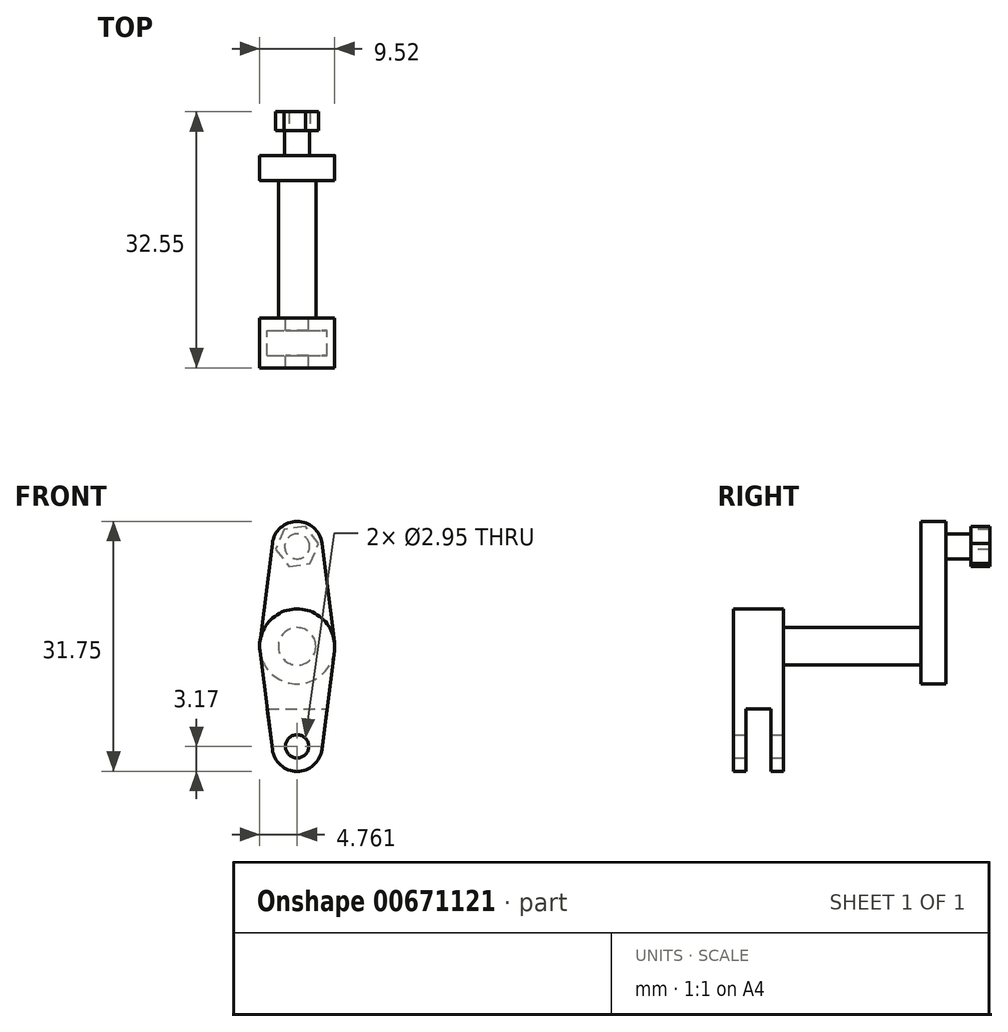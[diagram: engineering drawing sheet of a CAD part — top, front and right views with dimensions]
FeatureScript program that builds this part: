
annotation { "Feature Type Name" : "Feature", "Feature Type Description" : "" }
export const myFeature = defineFeature(function(context is Context, id is Id, definition is map)
    precondition{}
    {
        {
            var Q0;
            Q0=qCreatedBy(makeId("Front.planeOp"),FACE);
            var sketch = newSketch(context, id + "F0", { "sketchPlane" : qUnion([Q0])});
            skLineSegment(sketch, "E0.bottom", {"start": v(30.87, 50.07) * mm, "end": v(40.4, 50.07) * mm});
            skLineSegment(sketch, "E0.top", {"start": v(30.87, 15.15) * mm, "end": v(40.4, 15.15) * mm});
            skLineSegment(sketch, "E0.left", {"start": v(30.87, 50.07) * mm, "end": v(30.87, 15.15) * mm});
            skLineSegment(sketch, "E0.right", {"start": v(40.4, 50.07) * mm, "end": v(40.4, 15.15) * mm});
            skCircle(sketch, "E1", {"center": v(35.63, 45.31) * mm, "radius": 1.47 * mm});
            skCircle(sketch, "E2", {"center": v(35.63, 19.91) * mm, "radius": 1.47 * mm});
            skCircle(sketch, "E3", {"center": v(35.63, 32.61) * mm, "radius": 4.76 * mm});
            skCircle(sketch, "E4", {"center": v(35.63, 45.31) * mm, "radius": 3.18 * mm});
            skCircle(sketch, "E5", {"center": v(35.63, 19.91) * mm, "radius": 3.18 * mm});
            skLineSegment(sketch, "E6", {"start": v(32.48, 45.7) * mm, "end": v(30.9, 33.2) * mm});
            skLineSegment(sketch, "E7", {"start": v(38.78, 45.7) * mm, "end": v(40.36, 33.2) * mm});
            skLineSegment(sketch, "E8", {"start": v(30.9, 32.01) * mm, "end": v(32.48, 19.51) * mm});
            skLineSegment(sketch, "E9", {"start": v(40.36, 32.01) * mm, "end": v(38.78, 19.51) * mm});
            skSolve(sketch);
        }
        {
            var Q0;
            Q0=makeQuery(id+"F0.imprint","IMPRINT",FACE,{"disambiguationData":[TD([[makeQuery(id+"F0.imprint","IMPRINT",EDGE,{"derivedFrom":sQuery(id+"F0.wireOp",EDGE,"E1")}),1.0]])]});
            var Q1;
            Q1=makeQuery(id+"F0.imprint","IMPRINT",FACE,{"disambiguationData":[TD([[makeQuery(id+"F0.imprint","IMPRINT",EDGE,{"derivedFrom":sQuery(id+"F0.wireOp",EDGE,"E1")}),-1.0]])]});
            var Q2;
            {var subQ0=sQuery(id+"F0.wireOp",EDGE,"E6");Q2=makeQuery(id+"F0.imprint","IMPRINT",FACE,{"disambiguationData":[TD([[makeQuery(id+"F0.imprint","IMPRINT",EDGE,{"derivedFrom":subQ0}),1.0]])]});}
            var Q3;
            {var subQ0=sQuery(id+"F0.wireOp",EDGE,"E3");var subQ4=makeQuery(id+"F0.imprint","INTERSECT",VERTEX,{"derivedFrom":[subQ0,sQuery(id+"F0.wireOp",EDGE,"E7")]});Q3=makeQuery(id+"F0.imprint","IMPRINT",FACE,{"disambiguationData":[TD([[makeQuery(id+"F0.imprint","IMPRINT",EDGE,{"disambiguationData":[TD([[subQ4,1.0]])],"derivedFrom":subQ0}),1.0]])]});}
            extrude(context, id + "F1", {"entities" : qUnion([Q0, Q1, Q2, Q3]), "depth" : 3.17 * mm});
        }
        {
            var Q0;
            Q0=makeQuery(id+"F1.opExtrude","CAP_FACE",FACE,{"disambiguationData":[OSD([sQuery(id+"F0.wireOp",EDGE,"E3"),sQuery(id+"F0.wireOp",EDGE,"E4"),sQuery(id+"F0.wireOp",EDGE,"E6"),sQuery(id+"F0.wireOp",EDGE,"E7")])],"isStart":true});
            var sketch = newSketch(context, id + "F2", { "sketchPlane" : qUnion([Q0])});
            skCircle(sketch, "E10", {"center": v(-35.63, 45.31) * mm, "radius": 1.59 * mm});
            skSolve(sketch);
        }
        {
            var Q0;
            Q0=qSketchRegion(id+"F2",true);
            extrude(context, id + "F3", {"entities" : qUnion([Q0]), "operationType" : NewBodyOperationType.ADD, "depth" : 3.17 * mm});
        }
        {
            var Q0;
            Q0=makeQuery(id+"F3.opExtrude","CAP_FACE",FACE,{"disambiguationData":[OSD([sQuery(id+"F2.wireOp",EDGE,"E10")])],"isStart":false});
            var sketch = newSketch(context, id + "F4", { "sketchPlane" : qUnion([Q0])});
            skCircle(sketch, "E11.cCircle", {"center": v(-35.63, 45.31) * mm, "radius": 2.38 * mm, "construction": true});
            skLineSegment(sketch, "E11.0", {"start": v(-32.9, 44.95) * mm, "end": v(-34.58, 42.77) * mm});
            skLineSegment(sketch, "E11.1", {"start": v(-34.58, 42.77) * mm, "end": v(-37.3, 43.13) * mm});
            skLineSegment(sketch, "E11.2", {"start": v(-37.3, 43.13) * mm, "end": v(-38.36, 45.67) * mm});
            skLineSegment(sketch, "E11.3", {"start": v(-38.36, 45.67) * mm, "end": v(-36.69, 47.85) * mm});
            skLineSegment(sketch, "E11.4", {"start": v(-36.69, 47.85) * mm, "end": v(-33.96, 47.5) * mm});
            skLineSegment(sketch, "E11.5", {"start": v(-33.96, 47.5) * mm, "end": v(-32.9, 44.95) * mm});
            skPoint(sketch, "E11.0.midPoint", {"position": v(-33.74, 43.86) * mm});
            skSolve(sketch);
        }
        {
            var Q0;
            Q0=qSketchRegion(id+"F4",true);
            extrude(context, id + "F5", {"entities" : qUnion([Q0]), "operationType" : NewBodyOperationType.ADD, "depth" : 2.38 * mm});
        }
        {
            var Q0;
            Q0=makeQuery(id+"F1.opExtrude","CAP_FACE",FACE,{"disambiguationData":[OSD([sQuery(id+"F0.wireOp",EDGE,"E3"),sQuery(id+"F0.wireOp",EDGE,"E4"),sQuery(id+"F0.wireOp",EDGE,"E6"),sQuery(id+"F0.wireOp",EDGE,"E7")])],"isStart":false});
            var sketch = newSketch(context, id + "F6", { "sketchPlane" : qUnion([Q0])});
            skCircle(sketch, "E12", {"center": v(35.63, 32.61) * mm, "radius": 2.38 * mm});
            skSolve(sketch);
        }
        {
            var Q0;
            Q0=qSketchRegion(id+"F6",true);
            extrude(context, id + "F7", {"entities" : qUnion([Q0]), "operationType" : NewBodyOperationType.ADD, "depth" : 17.46 * mm});
        }
        {
            var Q0;
            Q0=makeQuery(id+"F7.opExtrude","CAP_FACE",FACE,{"disambiguationData":[OSD([sQuery(id+"F6.wireOp",EDGE,"E12")])],"isStart":false});
            var sketch = newSketch(context, id + "F8", { "sketchPlane" : qUnion([Q0])});
            skCircle(sketch, "E13", {"center": v(35.63, 32.61) * mm, "radius": 4.76 * mm});
            skCircle(sketch, "E14", {"center": v(35.63, 19.91) * mm, "radius": 3.18 * mm});
            skLineSegment(sketch, "E15", {"start": v(30.9, 32.01) * mm, "end": v(32.48, 19.51) * mm});
            skLineSegment(sketch, "E16", {"start": v(40.36, 32.01) * mm, "end": v(38.78, 19.51) * mm});
            skCircle(sketch, "E17", {"center": v(35.63, 19.91) * mm, "radius": 1.47 * mm});
            skSolve(sketch);
        }
        {
            var Q0;
            Q0=qSketchRegion(id+"F8",true);
            extrude(context, id + "F9", {"entities" : qUnion([Q0]), "operationType" : NewBodyOperationType.ADD, "depth" : 6.35 * mm});
        }
        {
            var Q0;
            Q0=makeQuery(id+"F9.opExtrude","CAP_FACE",FACE,{"disambiguationData":[OSD([sQuery(id+"F8.wireOp",EDGE,"E13"),sQuery(id+"F8.wireOp",EDGE,"E14"),sQuery(id+"F8.wireOp",EDGE,"E15"),sQuery(id+"F8.wireOp",EDGE,"E16"),sQuery(id+"F8.wireOp",EDGE,"E17")])],"isStart":false});
            cPlane(context, id + "F10", {"entities" : qUnion([Q0]), "cplaneType" : CPlaneType.OFFSET, "offset" : 3.17 * mm, "oppositeDirection" : true, "width" : 152.4 * mm, "height" : 152.4 * mm});
        }
        {
            var Q0;
            Q0=qCreatedBy(id+"F10.planeOp",FACE);
            var sketch = newSketch(context, id + "F11", { "sketchPlane" : qUnion([Q0])});
            skLineSegment(sketch, "E18.0", {"start": v(40.36, 32.01) * mm, "end": v(38.78, 19.51) * mm});
            skLineSegment(sketch, "E19.0", {"start": v(30.9, 32.01) * mm, "end": v(32.48, 19.51) * mm});
            skCircle(sketch, "E20.0", {"center": v(35.63, 19.91) * mm, "radius": 1.47 * mm});
            skArc(sketch, "E21.0", {"start": v(32.48, 19.51) * mm, "mid": v(35.63, 16.74) * mm, "end": v(38.78, 19.51) * mm});
            skLineSegment(sketch, "E22", {"start": v(31.83, 24.67) * mm, "end": v(39.43, 24.67) * mm});
            skSolve(sketch);
        }
        {
            var Q0;
            Q0=qSketchRegion(id+"F11",true);
            extrude(context, id + "F12", {"entities" : qUnion([Q0]), "operationType" : NewBodyOperationType.REMOVE, "endBound" : BoundingType.SYMMETRIC, "depth" : 3.17 * mm});
        }
    });
